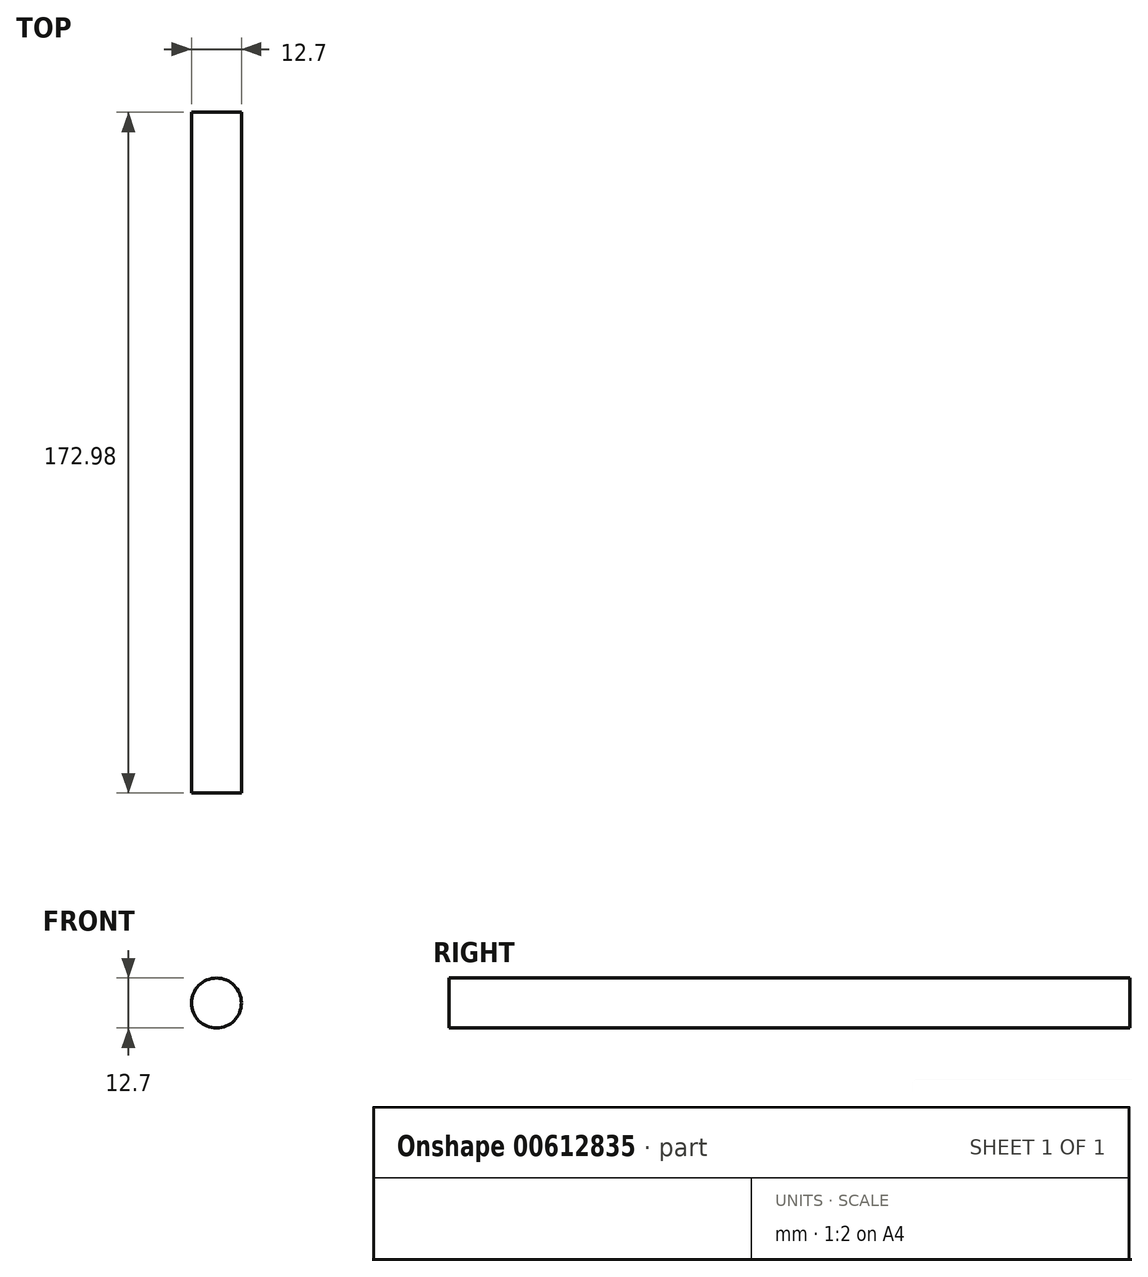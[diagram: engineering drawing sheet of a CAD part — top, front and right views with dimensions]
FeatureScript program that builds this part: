
annotation { "Feature Type Name" : "Feature", "Feature Type Description" : "" }
export const myFeature = defineFeature(function(context is Context, id is Id, definition is map)
    precondition{}
    {
        {
            var Q0;
            Q0=qCreatedBy(makeId("Front.planeOp"),FACE);
            var sketch = newSketch(context, id + "F0", { "sketchPlane" : qUnion([Q0])});
            skCircle(sketch, "E0", {"center": v(0, 0) * mm, "radius": 6.35 * mm});
            skSolve(sketch);
        }
        {
            var Q0;
            Q0=qSketchRegion(id+"F0",true);
            extrude(context, id + "F1", {"entities" : qUnion([Q0]), "depth" : 172.97 * mm, "symmetric" : true});
        }
    });
